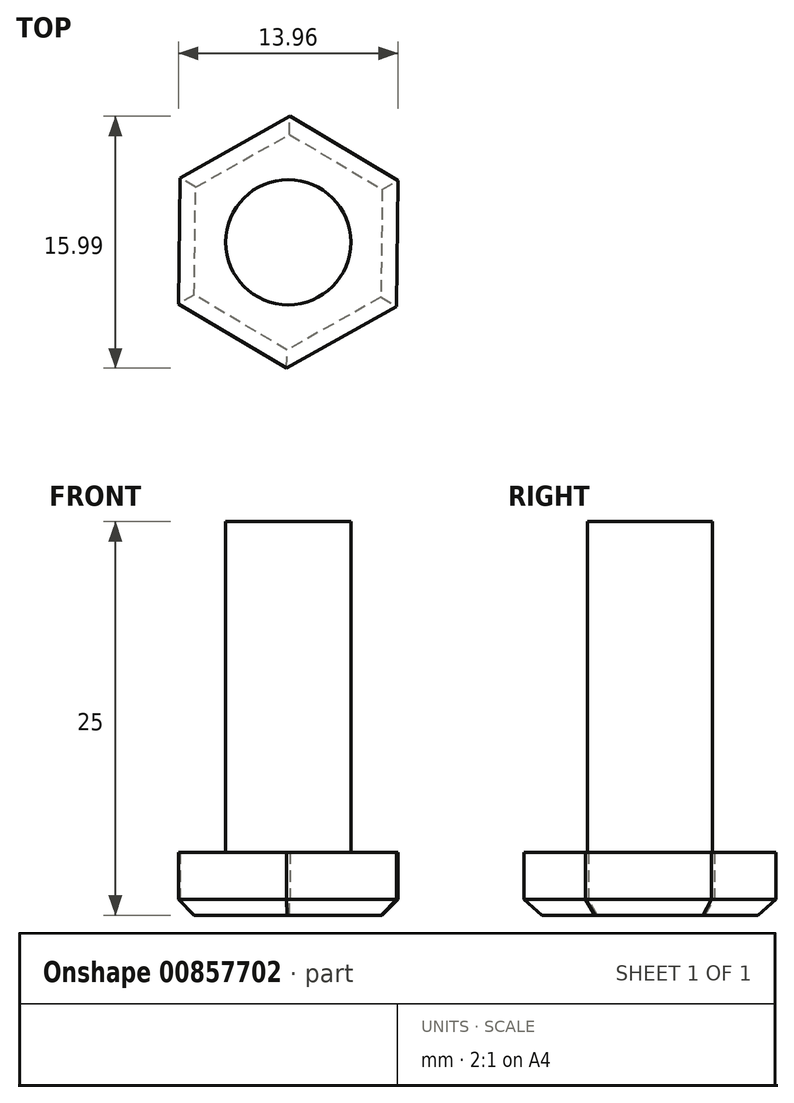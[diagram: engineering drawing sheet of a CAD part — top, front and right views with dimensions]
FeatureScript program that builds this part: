
annotation { "Feature Type Name" : "Feature", "Feature Type Description" : "" }
export const myFeature = defineFeature(function(context is Context, id is Id, definition is map)
    precondition{}
    {
        {
            var Q0;
            Q0=qCreatedBy(makeId("Top.planeOp"),FACE);
            var sketch = newSketch(context, id + "F0", { "sketchPlane" : qUnion([Q0])});
            skCircle(sketch, "E0.cCircle", {"center": v(-61.59, -9.17) * mm, "radius": 8 * mm, "construction": true});
            skLineSegment(sketch, "E0.0", {"start": v(-54.7, -13.25) * mm, "end": v(-61.69, -17.16) * mm});
            skLineSegment(sketch, "E0.1", {"start": v(-61.69, -17.16) * mm, "end": v(-68.57, -13.08) * mm});
            skLineSegment(sketch, "E0.2", {"start": v(-68.57, -13.08) * mm, "end": v(-68.47, -5.08) * mm});
            skLineSegment(sketch, "E0.3", {"start": v(-68.47, -5.08) * mm, "end": v(-61.5, -1.17) * mm});
            skLineSegment(sketch, "E0.4", {"start": v(-61.5, -1.17) * mm, "end": v(-54.61, -5.25) * mm});
            skLineSegment(sketch, "E0.5", {"start": v(-54.61, -5.25) * mm, "end": v(-54.7, -13.25) * mm});
            skCircle(sketch, "E1", {"center": v(-61.59, -9.17) * mm, "radius": 3.98 * mm});
            skSolve(sketch);
        }
        {
            var Q0;
            Q0=makeQuery(id+"F0.imprint","IMPRINT",FACE,{"disambiguationData":[TD([[makeQuery(id+"F0.imprint","IMPRINT",EDGE,{"derivedFrom":sQuery(id+"F0.wireOp",EDGE,"E1")}),1.0]])]});
            extrude(context, id + "F1", {"entities" : qUnion([Q0]), "depth" : 25 * mm, "offsetDistance" : 25 * mm});
        }
        {
            var Q0;
            Q0=makeQuery(id+"F0.imprint","IMPRINT",FACE,{"disambiguationData":[TD([[makeQuery(id+"F0.imprint","IMPRINT",EDGE,{"derivedFrom":sQuery(id+"F0.wireOp",EDGE,"E0.0")}),-1.0]])]});
            extrude(context, id + "F2", {"entities" : qUnion([Q0]), "operationType" : NewBodyOperationType.ADD, "depth" : 4 * mm, "offsetDistance" : 25 * mm});
        }
        {
            var Q0;
            {var subQ0=sQuery(id+"F0.wireOp",EDGE,"E1");Q0=makeQuery(id+"F2.boolean.opBoolean","MERGE",FACE,{"derivedFrom":[makeQuery(id+"F1.opExtrude","CAP_FACE",FACE,{"disambiguationData":[OSD([subQ0])],"isStart":true}),makeQuery(id+"F2.opExtrude","CAP_FACE",FACE,{"disambiguationData":[OSD([sQuery(id+"F0.wireOp",EDGE,"E0.0"),sQuery(id+"F0.wireOp",EDGE,"E0.1"),sQuery(id+"F0.wireOp",EDGE,"E0.2"),sQuery(id+"F0.wireOp",EDGE,"E0.3"),sQuery(id+"F0.wireOp",EDGE,"E0.4"),sQuery(id+"F0.wireOp",EDGE,"E0.5"),subQ0])],"isStart":true})]});}
            chamfer(context, id + "F3", {"entities" : qUnion([Q0]), "width" : 1 * mm, "tangentPropagation" : true});
        }
    });
